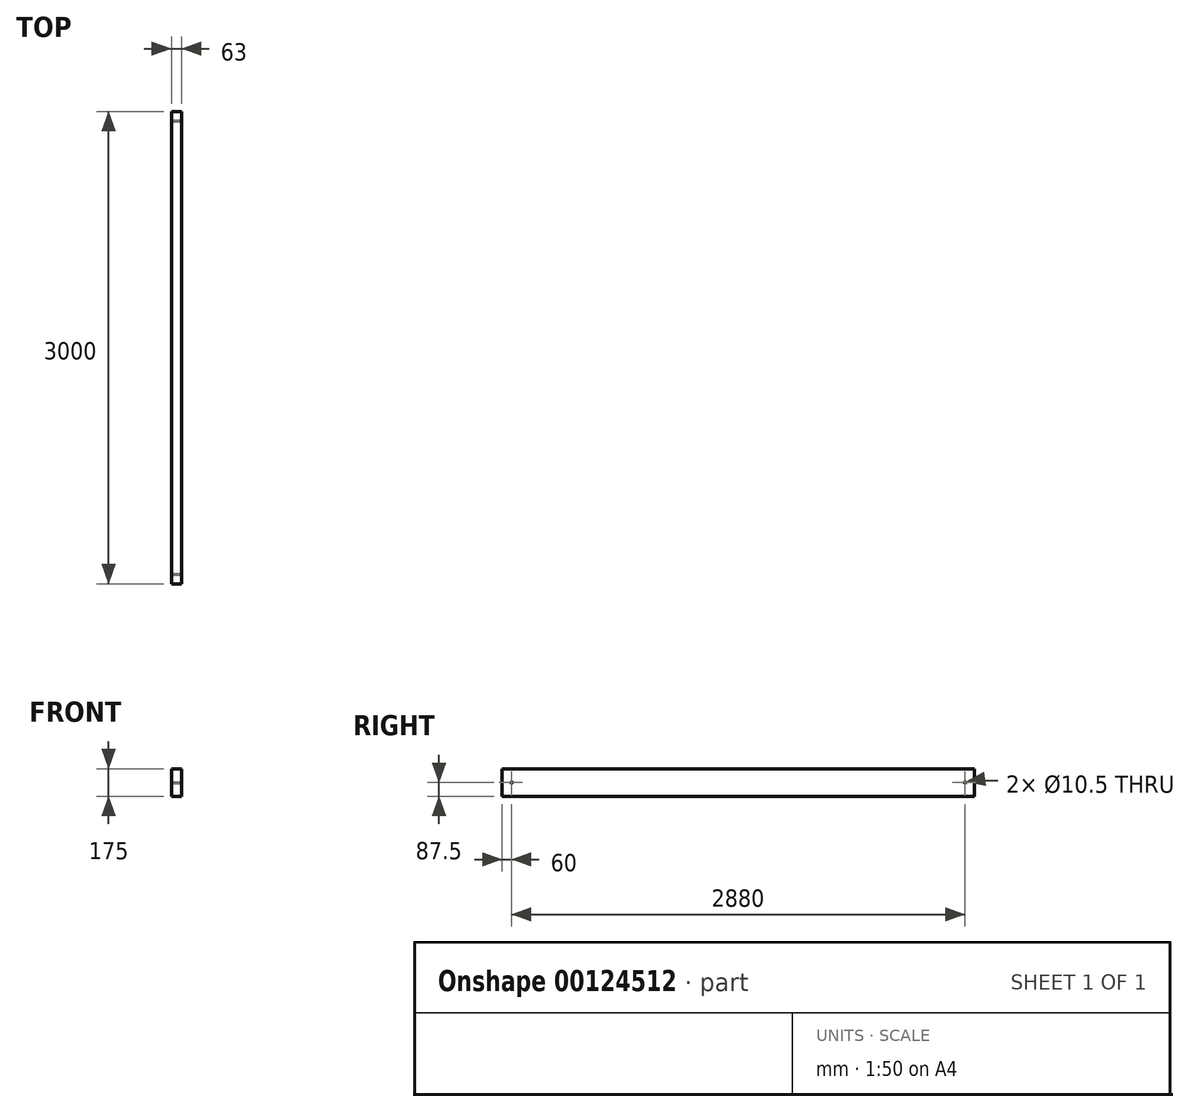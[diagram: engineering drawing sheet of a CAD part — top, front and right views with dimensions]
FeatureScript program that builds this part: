
annotation { "Feature Type Name" : "Feature", "Feature Type Description" : "" }
export const myFeature = defineFeature(function(context is Context, id is Id, definition is map)
    precondition{}
    {
        {
            var Q0;
            Q0=qCreatedBy(makeId("Front.planeOp"),FACE);
            var sketch = newSketch(context, id + "F0", { "sketchPlane" : qUnion([Q0])});
            skLineSegment(sketch, "E0.bottom", {"start": v(31.5, 87.5) * mm, "end": v(-31.5, 87.5) * mm});
            skLineSegment(sketch, "E0.top", {"start": v(31.5, -87.5) * mm, "end": v(-31.5, -87.5) * mm});
            skLineSegment(sketch, "E0.left", {"start": v(31.5, 87.5) * mm, "end": v(31.5, -87.5) * mm});
            skLineSegment(sketch, "E0.right", {"start": v(-31.5, 87.5) * mm, "end": v(-31.5, -87.5) * mm});
            skPoint(sketch, "E0.middle", {"position": v(0, 0) * mm});
            skSolve(sketch);
        }
        {
            var Q0;
            Q0=qSketchRegion(id+"F0",true);
            extrude(context, id + "F1", {"entities" : qUnion([Q0]), "endBound" : BoundingType.SYMMETRIC, "depth" : 3000 * mm});
        }
        {
            var Q0;
            Q0=makeQuery(id+"F1.opExtrude","SWEPT_FACE",FACE,{"disambiguationData":[OSD([sQuery(id+"F0.wireOp",EDGE,"E0.left")])]});
            var sketch = newSketch(context, id + "F2", { "sketchPlane" : qUnion([Q0])});
            skCircle(sketch, "E1", {"center": v(-1440, 0) * mm, "radius": 5.25 * mm});
            skCircle(sketch, "E2", {"center": v(1440, 0) * mm, "radius": 5.25 * mm});
            skSolve(sketch);
        }
        {
            var Q0;
            Q0 = qSketchRegion(id + "F2", true);
            extrude(context, id + "F3", {"entities" : qUnion([Q0]), "operationType" : NewBodyOperationType.REMOVE, "endBound" : BoundingType.THROUGH_ALL, "oppositeDirection" : true, "depth" : 25 * mm});
        }
    });
